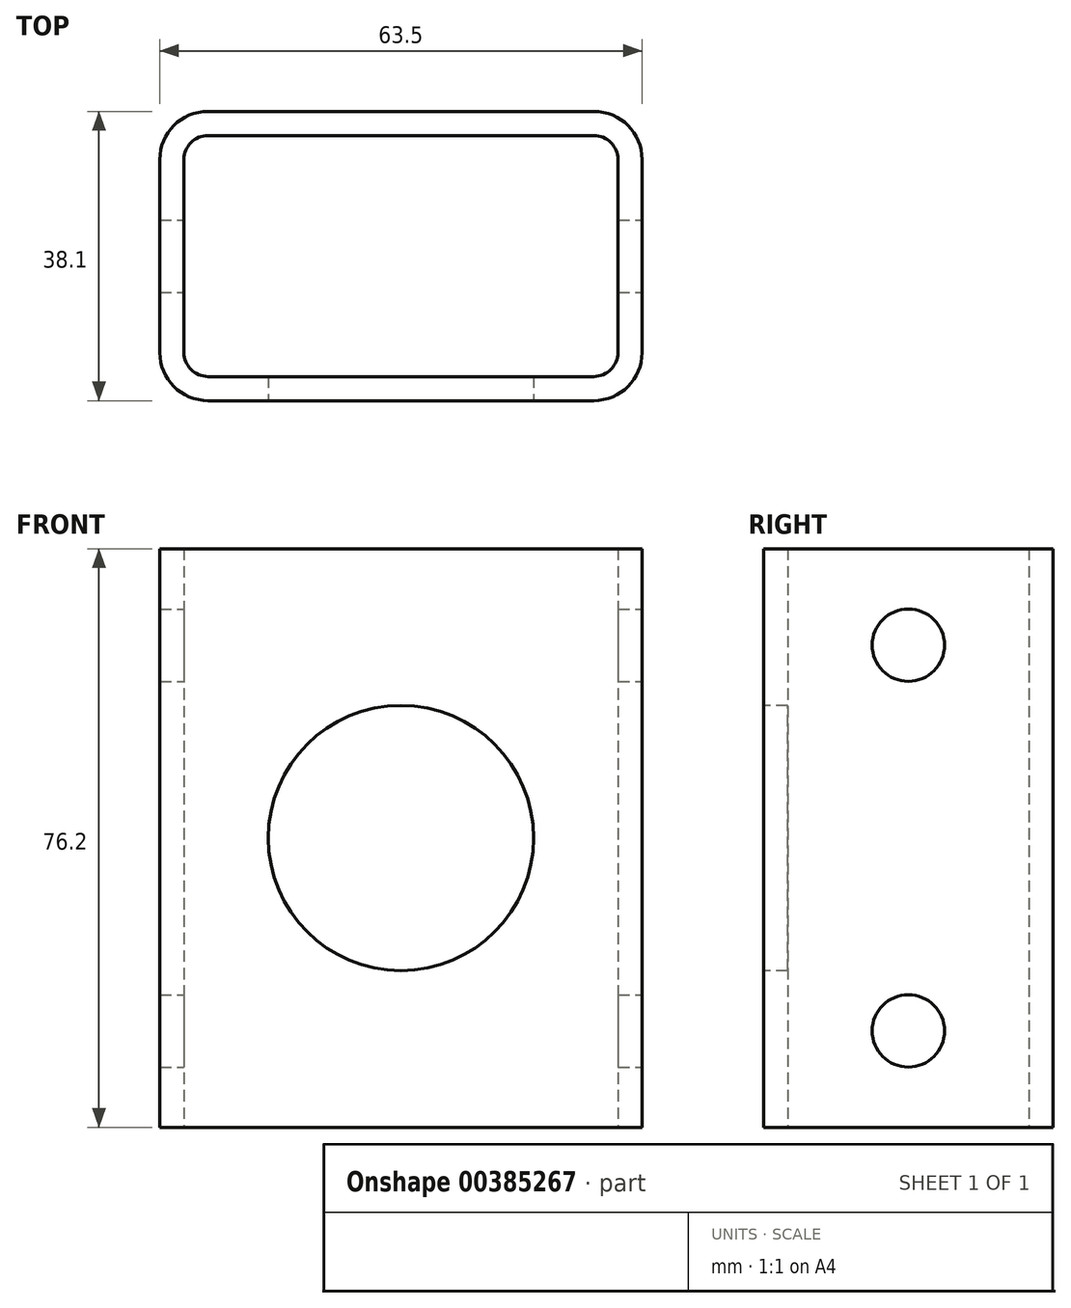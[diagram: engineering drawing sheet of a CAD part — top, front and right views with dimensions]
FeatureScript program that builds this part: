
annotation { "Feature Type Name" : "Feature", "Feature Type Description" : "" }
export const myFeature = defineFeature(function(context is Context, id is Id, definition is map)
    precondition{}
    {
        {
            var Q0;
            Q0=qCreatedBy(makeId("Top.planeOp"),FACE);
            var sketch = newSketch(context, id + "F0", { "sketchPlane" : qUnion([Q0])});
            skLineSegment(sketch, "E0.bottom", {"start": v(25.4, -19.05) * mm, "end": v(-25.4, -19.05) * mm});
            skLineSegment(sketch, "E0.top", {"start": v(25.4, 19.05) * mm, "end": v(-25.4, 19.05) * mm});
            skLineSegment(sketch, "E0.left", {"start": v(31.75, -12.7) * mm, "end": v(31.75, 12.7) * mm});
            skLineSegment(sketch, "E0.right", {"start": v(-31.75, -12.7) * mm, "end": v(-31.75, 12.7) * mm});
            skPoint(sketch, "E0.middle", {"position": v(0, 0) * mm});
            skPoint(sketch, "E1.visualSharp", {"position": v(-31.75, 19.05) * mm});
            skArc(sketch, "E1.filletArc", {"start": v(-25.4, 19.05) * mm, "mid": v(-29.9, 17.2) * mm, "end": v(-31.75, 12.7) * mm});
            skPoint(sketch, "E2.visualSharp", {"position": v(31.75, 19.05) * mm});
            skArc(sketch, "E2.filletArc", {"start": v(31.75, 12.7) * mm, "mid": v(29.9, 17.2) * mm, "end": v(25.4, 19.05) * mm});
            skPoint(sketch, "E3.visualSharp", {"position": v(31.75, -19.05) * mm});
            skArc(sketch, "E3.filletArc", {"start": v(25.4, -19.05) * mm, "mid": v(29.9, -17.2) * mm, "end": v(31.75, -12.7) * mm});
            skPoint(sketch, "E4.visualSharp", {"position": v(-31.75, -19.05) * mm});
            skArc(sketch, "E4.filletArc", {"start": v(-31.75, -12.7) * mm, "mid": v(-29.9, -17.2) * mm, "end": v(-25.4, -19.05) * mm});
            skLineSegment(sketch, "E5.0", {"start": v(25.4, 15.88) * mm, "end": v(-25.4, 15.87) * mm});
            skLineSegment(sketch, "E6.0", {"start": v(28.57, -12.7) * mm, "end": v(28.57, 12.7) * mm});
            skLineSegment(sketch, "E7.0", {"start": v(25.4, -15.88) * mm, "end": v(-25.4, -15.88) * mm});
            skLineSegment(sketch, "E8.0", {"start": v(-28.57, -12.7) * mm, "end": v(-28.57, 12.7) * mm});
            skPoint(sketch, "E9.visualSharp", {"position": v(-28.57, 15.87) * mm});
            skArc(sketch, "E9.filletArc", {"start": v(-25.4, 15.87) * mm, "mid": v(-27.65, 14.95) * mm, "end": v(-28.57, 12.7) * mm});
            skPoint(sketch, "E10.visualSharp", {"position": v(28.57, 15.88) * mm});
            skArc(sketch, "E10.filletArc", {"start": v(28.57, 12.7) * mm, "mid": v(27.65, 14.95) * mm, "end": v(25.4, 15.88) * mm});
            skPoint(sketch, "E11.visualSharp", {"position": v(28.57, -15.88) * mm});
            skArc(sketch, "E11.filletArc", {"start": v(25.4, -15.88) * mm, "mid": v(27.65, -14.95) * mm, "end": v(28.57, -12.7) * mm});
            skPoint(sketch, "E12.visualSharp", {"position": v(-28.57, -15.88) * mm});
            skArc(sketch, "E12.filletArc", {"start": v(-28.57, -12.7) * mm, "mid": v(-27.65, -14.95) * mm, "end": v(-25.4, -15.88) * mm});
            skSolve(sketch);
        }
        {
            var Q0;
            Q0=makeQuery(id+"F0.imprint","IMPRINT",FACE,{"disambiguationData":[TD([[makeQuery(id+"F0.imprint","IMPRINT",EDGE,{"derivedFrom":sQuery(id+"F0.wireOp",EDGE,"E0.bottom")}),-1.0]])]});
            extrude(context, id + "F1", {"entities" : qUnion([Q0]), "endBound" : BoundingType.SYMMETRIC, "depth" : 76.2 * mm});
        }
        {
            var Q0;
            Q0=makeQuery(id+"F1.opExtrude","SWEPT_FACE",FACE,{"disambiguationData":[OSD([sQuery(id+"F0.wireOp",EDGE,"E0.left")])]});
            var sketch = newSketch(context, id + "F2", { "sketchPlane" : qUnion([Q0])});
            skCircle(sketch, "E13", {"center": v(0, 25.4) * mm, "radius": 4.76 * mm});
            skCircle(sketch, "E14", {"center": v(0, -25.4) * mm, "radius": 4.76 * mm});
            skSolve(sketch);
        }
        {
            var Q0;
            Q0=makeQuery(id+"F2.imprint","IMPRINT",FACE,{"disambiguationData":[TD([[makeQuery(id+"F2.imprint","IMPRINT",EDGE,{"derivedFrom":sQuery(id+"F2.wireOp",EDGE,"E13")}),1.0]])]});
            var Q1;
            Q1=makeQuery(id+"F2.imprint","IMPRINT",FACE,{"disambiguationData":[TD([[makeQuery(id+"F2.imprint","IMPRINT",EDGE,{"derivedFrom":sQuery(id+"F2.wireOp",EDGE,"E14")}),1.0]])]});
            var Q2;
            Q2=sQuery(id+"F2.wireOp",EDGE,"E13");
            var Q3;
            Q3=sQuery(id+"F2.wireOp",EDGE,"E14");
            extrude(context, id + "F3", {"entities" : qUnion([Q0, Q1]), "operationType" : NewBodyOperationType.REMOVE, "surfaceEntities" : qUnion([Q2, Q3]), "endBound" : BoundingType.THROUGH_ALL, "oppositeDirection" : true, "depth" : 25.4 * mm});
        }
        {
            var Q0;
            Q0=makeQuery(id+"F1.opExtrude","SWEPT_FACE",FACE,{"disambiguationData":[OSD([sQuery(id+"F0.wireOp",EDGE,"E0.bottom")])]});
            var sketch = newSketch(context, id + "F4", { "sketchPlane" : qUnion([Q0])});
            skCircle(sketch, "E15", {"center": v(0, 0) * mm, "radius": 17.46 * mm});
            skSolve(sketch);
        }
        {
            var Q0;
            Q0=makeQuery(id+"F4.imprint","IMPRINT",FACE,{"disambiguationData":[TD([[makeQuery(id+"F4.imprint","IMPRINT",EDGE,{"derivedFrom":sQuery(id+"F4.wireOp",EDGE,"E15")}),1.0]])]});
            extrude(context, id + "F5", {"entities" : qUnion([Q0]), "operationType" : NewBodyOperationType.REMOVE, "endBound" : BoundingType.UP_TO_NEXT, "oppositeDirection" : true, "depth" : 25.4 * mm});
        }
    });
